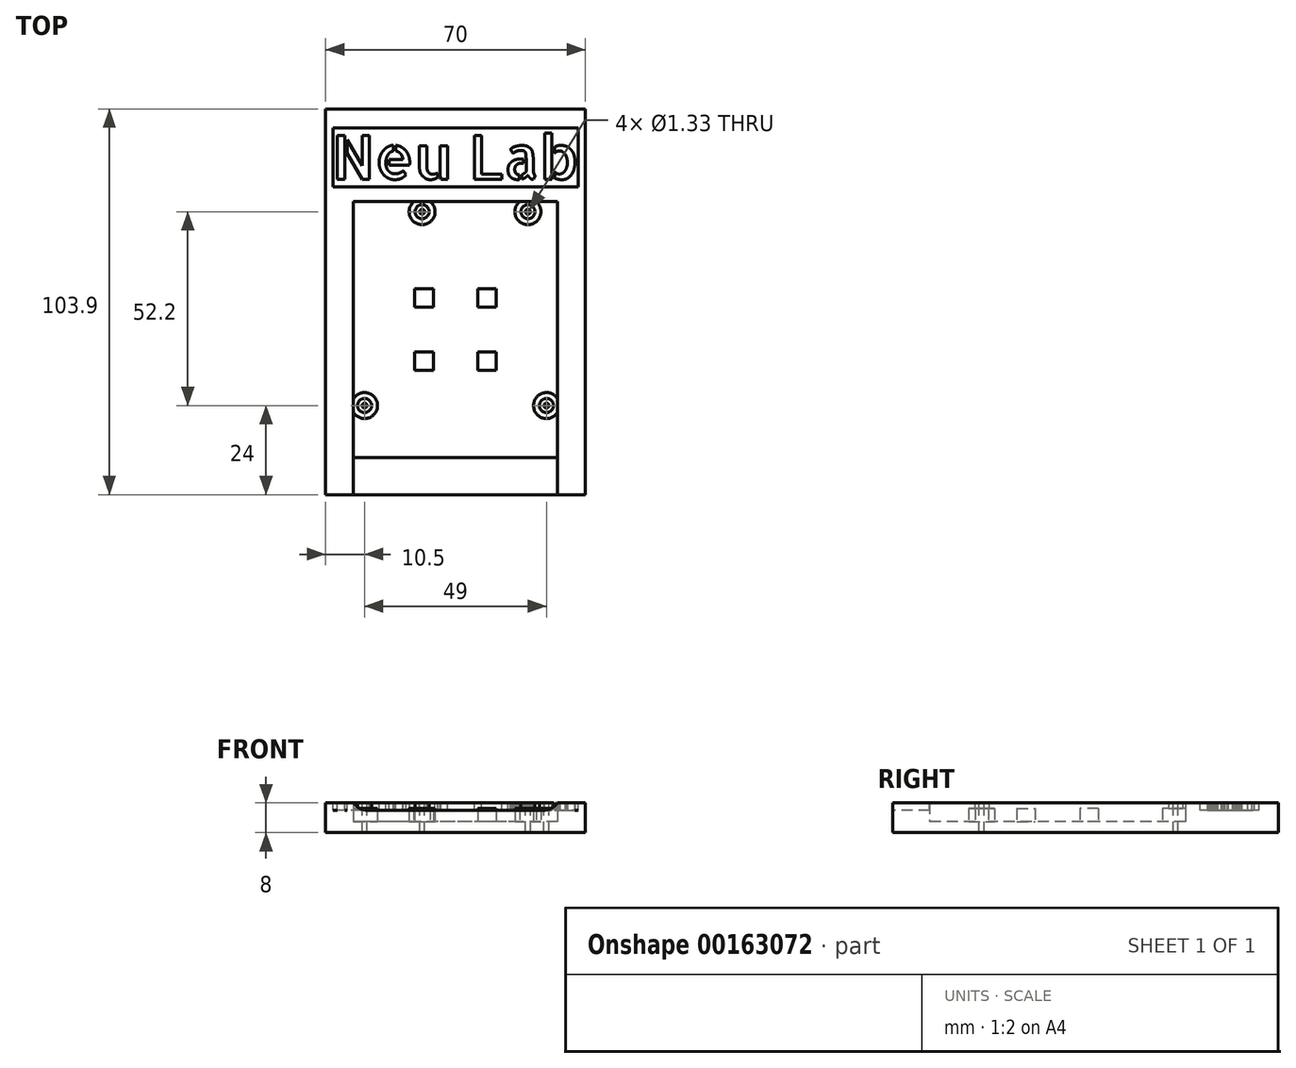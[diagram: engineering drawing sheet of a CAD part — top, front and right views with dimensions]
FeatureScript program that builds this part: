
annotation { "Feature Type Name" : "Feature", "Feature Type Description" : "" }
export const myFeature = defineFeature(function(context is Context, id is Id, definition is map)
    precondition{}
    {
        {
            var Q0;
            Q0=qCreatedBy(makeId("Top.planeOp"),FACE);
            var sketch = newSketch(context, id + "F0", { "sketchPlane" : qUnion([Q0])});
            skLineSegment(sketch, "E0.bottom", {"start": v(27.5, 34.45) * mm, "end": v(-27.5, 34.45) * mm});
            skLineSegment(sketch, "E0.top", {"start": v(27.5, -34.45) * mm, "end": v(-27.5, -34.45) * mm});
            skLineSegment(sketch, "E0.left", {"start": v(27.5, 34.45) * mm, "end": v(27.5, -34.45) * mm});
            skLineSegment(sketch, "E0.right", {"start": v(-27.5, 34.45) * mm, "end": v(-27.5, -34.45) * mm});
            skPoint(sketch, "E0.middle", {"position": v(0, 0) * mm});
            skLineSegment(sketch, "E1.top", {"start": v(35, -44.45) * mm, "end": v(-35, -44.45) * mm});
            skLineSegment(sketch, "E1.left", {"start": v(35, 44.45) * mm, "end": v(35, -44.45) * mm});
            skLineSegment(sketch, "E1.right", {"start": v(-35, 44.45) * mm, "end": v(-35, -44.45) * mm});
            skCircle(sketch, "E2", {"center": v(-9, 31.75) * mm, "radius": 1.9 * mm});
            skCircle(sketch, "E3", {"center": v(19.5, 31.75) * mm, "radius": 1.9 * mm});
            skCircle(sketch, "E4", {"center": v(-24.5, -20.45) * mm, "radius": 1.9 * mm});
            skCircle(sketch, "E5", {"center": v(24.5, -20.45) * mm, "radius": 1.9 * mm});
            skLineSegment(sketch, "E6.top", {"start": v(-35, 59.45) * mm, "end": v(35, 59.45) * mm});
            skLineSegment(sketch, "E6.left", {"start": v(-35, 44.45) * mm, "end": v(-35, 59.45) * mm});
            skLineSegment(sketch, "E6.right", {"start": v(35, 44.45) * mm, "end": v(35, 59.45) * mm});
            skArc(sketch, "E7", {"start": v(-11.23, 34.45) * mm, "mid": v(-9, 28.25) * mm, "end": v(-6.77, 34.45) * mm});
            skArc(sketch, "E8", {"start": v(17.27, 34.45) * mm, "mid": v(19.5, 28.25) * mm, "end": v(21.73, 34.45) * mm});
            skArc(sketch, "E9", {"start": v(-27.5, -22.25) * mm, "mid": v(-21, -20.45) * mm, "end": v(-27.5, -18.65) * mm});
            skArc(sketch, "E10", {"start": v(27.5, -18.65) * mm, "mid": v(21, -20.45) * mm, "end": v(27.5, -22.25) * mm});
            skCircle(sketch, "E11", {"center": v(-9, 31.75) * mm, "radius": 0.67 * mm});
            skCircle(sketch, "E12", {"center": v(19.5, 31.75) * mm, "radius": 0.67 * mm});
            skCircle(sketch, "E13", {"center": v(-24.5, -20.45) * mm, "radius": 0.67 * mm});
            skCircle(sketch, "E14", {"center": v(24.5, -20.45) * mm, "radius": 0.67 * mm});
            skSolve(sketch);
        }
        {
            var Q0;
            {var subQ8=sQuery(id+"F0.wireOp",EDGE,"E0.top");Q0=makeQuery(id+"F0.imprint","IMPRINT",FACE,{"disambiguationData":[TD([[makeQuery(id+"F0.imprint","IMPRINT",EDGE,{"derivedFrom":subQ8}),1.0]])]});}
            var Q1;
            {var subQ1=sQuery(id+"F0.wireOp",EDGE,"E0.top");Q1=makeQuery(id+"F0.imprint","IMPRINT",FACE,{"disambiguationData":[TD([[makeQuery(id+"F0.imprint","IMPRINT",EDGE,{"derivedFrom":subQ1}),-1.0]])]});}
            var Q2;
            Q2=makeQuery(id+"F0.imprint","IMPRINT",FACE,{"disambiguationData":[TD([[makeQuery(id+"F0.imprint","IMPRINT",EDGE,{"derivedFrom":sQuery(id+"F0.wireOp",EDGE,"E4")}),-1.0]])]});
            var Q3;
            Q3=makeQuery(id+"F0.imprint","IMPRINT",FACE,{"disambiguationData":[TD([[makeQuery(id+"F0.imprint","IMPRINT",EDGE,{"derivedFrom":sQuery(id+"F0.wireOp",EDGE,"E4")}),1.0]])]});
            var Q4;
            Q4=makeQuery(id+"F0.imprint","IMPRINT",FACE,{"disambiguationData":[TD([[makeQuery(id+"F0.imprint","IMPRINT",EDGE,{"derivedFrom":sQuery(id+"F0.wireOp",EDGE,"E5")}),-1.0]])]});
            var Q5;
            Q5=makeQuery(id+"F0.imprint","IMPRINT",FACE,{"disambiguationData":[TD([[makeQuery(id+"F0.imprint","IMPRINT",EDGE,{"derivedFrom":sQuery(id+"F0.wireOp",EDGE,"E5")}),1.0]])]});
            var Q6;
            Q6=makeQuery(id+"F0.imprint","IMPRINT",FACE,{"disambiguationData":[TD([[makeQuery(id+"F0.imprint","IMPRINT",EDGE,{"derivedFrom":sQuery(id+"F0.wireOp",EDGE,"E2")}),-1.0]])]});
            var Q7;
            Q7=makeQuery(id+"F0.imprint","IMPRINT",FACE,{"disambiguationData":[TD([[makeQuery(id+"F0.imprint","IMPRINT",EDGE,{"derivedFrom":sQuery(id+"F0.wireOp",EDGE,"E2")}),1.0]])]});
            var Q8;
            Q8=makeQuery(id+"F0.imprint","IMPRINT",FACE,{"disambiguationData":[TD([[makeQuery(id+"F0.imprint","IMPRINT",EDGE,{"derivedFrom":sQuery(id+"F0.wireOp",EDGE,"E3")}),-1.0]])]});
            var Q9;
            Q9=makeQuery(id+"F0.imprint","IMPRINT",FACE,{"disambiguationData":[TD([[makeQuery(id+"F0.imprint","IMPRINT",EDGE,{"derivedFrom":sQuery(id+"F0.wireOp",EDGE,"E3")}),1.0]])]});
            extrude(context, id + "F1", {"entities" : qUnion([Q0, Q1, Q2, Q3, Q4, Q5, Q6, Q7, Q8, Q9]), "oppositeDirection" : true, "depth" : 3 * mm});
        }
        {
            var Q0;
            {var subQ8=sQuery(id+"F0.wireOp",EDGE,"E0.top");Q0=makeQuery(id+"F0.imprint","IMPRINT",FACE,{"disambiguationData":[TD([[makeQuery(id+"F0.imprint","IMPRINT",EDGE,{"derivedFrom":subQ8}),1.0]])]});}
            extrude(context, id + "F2", {"entities" : qUnion([Q0]), "operationType" : NewBodyOperationType.ADD, "depth" : 5 * mm});
        }
        {
            var Q0;
            Q0=makeQuery(id+"F0.imprint","IMPRINT",FACE,{"disambiguationData":[TD([[makeQuery(id+"F0.imprint","IMPRINT",EDGE,{"derivedFrom":sQuery(id+"F0.wireOp",EDGE,"E3")}),-1.0]])]});
            var Q1;
            Q1=makeQuery(id+"F0.imprint","IMPRINT",FACE,{"disambiguationData":[TD([[makeQuery(id+"F0.imprint","IMPRINT",EDGE,{"derivedFrom":sQuery(id+"F0.wireOp",EDGE,"E2")}),-1.0]])]});
            var Q2;
            Q2=makeQuery(id+"F0.imprint","IMPRINT",FACE,{"disambiguationData":[TD([[makeQuery(id+"F0.imprint","IMPRINT",EDGE,{"derivedFrom":sQuery(id+"F0.wireOp",EDGE,"E4")}),-1.0]])]});
            var Q3;
            Q3=makeQuery(id+"F0.imprint","IMPRINT",FACE,{"disambiguationData":[TD([[makeQuery(id+"F0.imprint","IMPRINT",EDGE,{"derivedFrom":sQuery(id+"F0.wireOp",EDGE,"E5")}),-1.0]])]});
            extrude(context, id + "F3", {"entities" : qUnion([Q0, Q1, Q2, Q3]), "operationType" : NewBodyOperationType.ADD, "depth" : 3.5 * mm});
        }
        {
            var Q0;
            Q0=makeQuery(id+"F0.imprint","IMPRINT",FACE,{"disambiguationData":[TD([[makeQuery(id+"F0.imprint","IMPRINT",EDGE,{"derivedFrom":sQuery(id+"F0.wireOp",EDGE,"E2")}),1.0]])]});
            var Q1;
            Q1=makeQuery(id+"F0.imprint","IMPRINT",FACE,{"disambiguationData":[TD([[makeQuery(id+"F0.imprint","IMPRINT",EDGE,{"derivedFrom":sQuery(id+"F0.wireOp",EDGE,"E3")}),1.0]])]});
            var Q2;
            Q2=makeQuery(id+"F0.imprint","IMPRINT",FACE,{"disambiguationData":[TD([[makeQuery(id+"F0.imprint","IMPRINT",EDGE,{"derivedFrom":sQuery(id+"F0.wireOp",EDGE,"E4")}),1.0]])]});
            var Q3;
            Q3=makeQuery(id+"F0.imprint","IMPRINT",FACE,{"disambiguationData":[TD([[makeQuery(id+"F0.imprint","IMPRINT",EDGE,{"derivedFrom":sQuery(id+"F0.wireOp",EDGE,"E5")}),1.0]])]});
            extrude(context, id + "F4", {"entities" : qUnion([Q0, Q1, Q2, Q3]), "operationType" : NewBodyOperationType.ADD, "depth" : 5 * mm});
        }
        {
            var Q0;
            {var subQ1=sQuery(id+"F0.wireOp",EDGE,"E0.top");Q0=makeQuery(id+"F0.imprint","IMPRINT",FACE,{"disambiguationData":[TD([[makeQuery(id+"F0.imprint","IMPRINT",EDGE,{"derivedFrom":subQ1}),-1.0]])]});}
            var sketch = newSketch(context, id + "F5", { "sketchPlane" : qUnion([Q0])});
            skLineSegment(sketch, "E15.bottom", {"start": v(-11, 11) * mm, "end": v(-6, 11) * mm});
            skLineSegment(sketch, "E15.top", {"start": v(-11, 6) * mm, "end": v(-6, 6) * mm});
            skLineSegment(sketch, "E15.left", {"start": v(-11, 11) * mm, "end": v(-11, 6) * mm});
            skLineSegment(sketch, "E15.right", {"start": v(-6, 11) * mm, "end": v(-6, 6) * mm});
            skLineSegment(sketch, "E16", {"start": v(0, 6.9) * mm, "end": v(0, -6.73) * mm, "construction": true});
            skLineSegment(sketch, "E17", {"start": v(-15.32, 0) * mm, "end": v(15.3, 0) * mm, "construction": true});
            skLineSegment(sketch, "E18.MirrorCS", {"start": v(11, 11) * mm, "end": v(11, 6) * mm});
            skLineSegment(sketch, "E19.MirrorCS", {"start": v(6, 11) * mm, "end": v(6, 6) * mm});
            skLineSegment(sketch, "E20.MirrorCS", {"start": v(11, 6) * mm, "end": v(6, 6) * mm});
            skLineSegment(sketch, "E21.MirrorCS", {"start": v(11, 11) * mm, "end": v(6, 11) * mm});
            skLineSegment(sketch, "E22.MirrorCS", {"start": v(-6, -11) * mm, "end": v(-6, -6) * mm});
            skLineSegment(sketch, "E23.MirrorCS", {"start": v(-11, -11) * mm, "end": v(-11, -6) * mm});
            skLineSegment(sketch, "E24.MirrorCS", {"start": v(-11, -6) * mm, "end": v(-6, -6) * mm});
            skLineSegment(sketch, "E25.MirrorCS", {"start": v(-11, -11) * mm, "end": v(-6, -11) * mm});
            skLineSegment(sketch, "E26.MirrorCS", {"start": v(11, -11) * mm, "end": v(11, -6) * mm});
            skLineSegment(sketch, "E27.MirrorCS", {"start": v(6, -11) * mm, "end": v(6, -6) * mm});
            skLineSegment(sketch, "E28.MirrorCS", {"start": v(11, -6) * mm, "end": v(6, -6) * mm});
            skLineSegment(sketch, "E29.MirrorCS", {"start": v(11, -11) * mm, "end": v(6, -11) * mm});
            skSolve(sketch);
        }
        {
            var Q0;
            Q0 = qSketchRegion(id + "F5", true);
            extrude(context, id + "F6", {"entities" : qUnion([Q0]), "operationType" : NewBodyOperationType.ADD, "depth" : 3.5 * mm});
        }
        {
            var Q0;
            {var subQ0=sQuery(id+"F0.wireOp",EDGE,"E1.top");Q0=makeQuery(id+"F2.boolean.opBoolean","MERGE",FACE,{"derivedFrom":[makeQuery(id+"F1.opExtrude","SWEPT_FACE",FACE,{"disambiguationData":[OSD([subQ0])]}),makeQuery(id+"F2.opExtrude","SWEPT_FACE",FACE,{"disambiguationData":[OSD([subQ0])]})]});}
            var sketch = newSketch(context, id + "F7", { "sketchPlane" : qUnion([Q0])});
            skLineSegment(sketch, "E30.bottom", {"start": v(-27.5, 5) * mm, "end": v(27.5, 5) * mm});
            skLineSegment(sketch, "E30.top", {"start": v(-27.5, 3) * mm, "end": v(27.5, 3) * mm});
            skLineSegment(sketch, "E30.left", {"start": v(-27.5, 5) * mm, "end": v(-27.5, 3) * mm});
            skLineSegment(sketch, "E30.right", {"start": v(27.5, 5) * mm, "end": v(27.5, 3) * mm});
            skSolve(sketch);
        }
        {
            var Q0;
            Q0=makeQuery(id+"F7.imprint","IMPRINT",FACE,{"disambiguationData":[TD([[makeQuery(id+"F7.imprint","IMPRINT",EDGE,{"derivedFrom":sQuery(id+"F7.wireOp",EDGE,"E30.bottom")}),1.0]])]});
            var Q1;
            Q1=makeQuery(id+"F2.opExtrude","SWEPT_FACE",FACE,{"disambiguationData":[OSD([sQuery(id+"F0.wireOp",EDGE,"E0.top")])]});
            extrude(context, id + "F8", {"entities" : qUnion([Q0]), "operationType" : NewBodyOperationType.REMOVE, "endBound" : BoundingType.UP_TO_SURFACE, "oppositeDirection" : true, "endBoundEntityFace" : qUnion([Q1]), "depth" : 25 * mm});
        }
        {
            var Q0;
            Q0=makeQuery(id+"F8.boolean.opBoolean","COPY",EDGE,{"derivedFrom":makeQuery(id+"F8.opExtrude","SWEPT_EDGE",EDGE,{"disambiguationData":[OSD([sQuery(id+"F7.wireOp",EDGE,"E30.top"),sQuery(id+"F7.wireOp",EDGE,"E30.right")])]})});
            var Q1;
            Q1=makeQuery(id+"F8.boolean.opBoolean","COPY",EDGE,{"derivedFrom":makeQuery(id+"F8.opExtrude","SWEPT_EDGE",EDGE,{"disambiguationData":[OSD([sQuery(id+"F7.wireOp",EDGE,"E30.top"),sQuery(id+"F7.wireOp",EDGE,"E30.left")])]})});
            fillet(context, id + "F9", {"entities" : qUnion([Q0, Q1]), "radius" : 5 * mm, "tangentPropagation" : true, "allowEdgeOverflow" : false});
        }
        {
            var Q0;
            Q0=makeQuery(id+"F2.opExtrude","CAP_FACE",FACE,{"disambiguationData":[OSD([sQuery(id+"F0.wireOp",EDGE,"E0.bottom"),sQuery(id+"F0.wireOp",EDGE,"E0.top"),sQuery(id+"F0.wireOp",EDGE,"E0.left"),sQuery(id+"F0.wireOp",EDGE,"E0.right"),sQuery(id+"F0.wireOp",EDGE,"E1.top"),sQuery(id+"F0.wireOp",EDGE,"E1.left"),sQuery(id+"F0.wireOp",EDGE,"E1.right"),sQuery(id+"F0.wireOp",EDGE,"E6.top"),sQuery(id+"F0.wireOp",EDGE,"E6.left"),sQuery(id+"F0.wireOp",EDGE,"E6.right")])],"isStart":false});
            var sketch = newSketch(context, id + "F10", { "sketchPlane" : qUnion([Q0])});
            skText(sketch, "E31", { "text": "Neu Lab", "fontName": "AllertaStencil-Regular.ttf"});
            skLineSegment(sketch, "E32.bottom", {"start": v(-33, 54.33) * mm, "end": v(33, 54.33) * mm});
            skLineSegment(sketch, "E32.top", {"start": v(-33, 38.45) * mm, "end": v(33, 38.45) * mm});
            skLineSegment(sketch, "E32.left", {"start": v(-33, 54.33) * mm, "end": v(-33, 38.45) * mm});
            skLineSegment(sketch, "E32.right", {"start": v(33, 54.33) * mm, "end": v(33, 38.45) * mm});
            const initialGuessF10  = {"E31": [-0.03328, 0.04045, 1, 0, 0.01188]};
            skSetInitialGuess(sketch, initialGuessF10);
            skSolve(sketch);
        }
        {
            var Q0;
            Q0=makeQuery(id+"F10.imprint","IMPRINT",FACE,{"disambiguationData":[TD([[makeQuery(id+"F10.imprint","IMPRINT",EDGE,{"derivedFrom":sQuery(id+"F10.wireOp",EDGE,"E31.sketch_text.stroke-0")}),1.0]])]});
            extrude(context, id + "F11", {"entities" : qUnion([Q0]), "operationType" : NewBodyOperationType.REMOVE, "oppositeDirection" : true, "depth" : 2 * mm});
        }
    });
